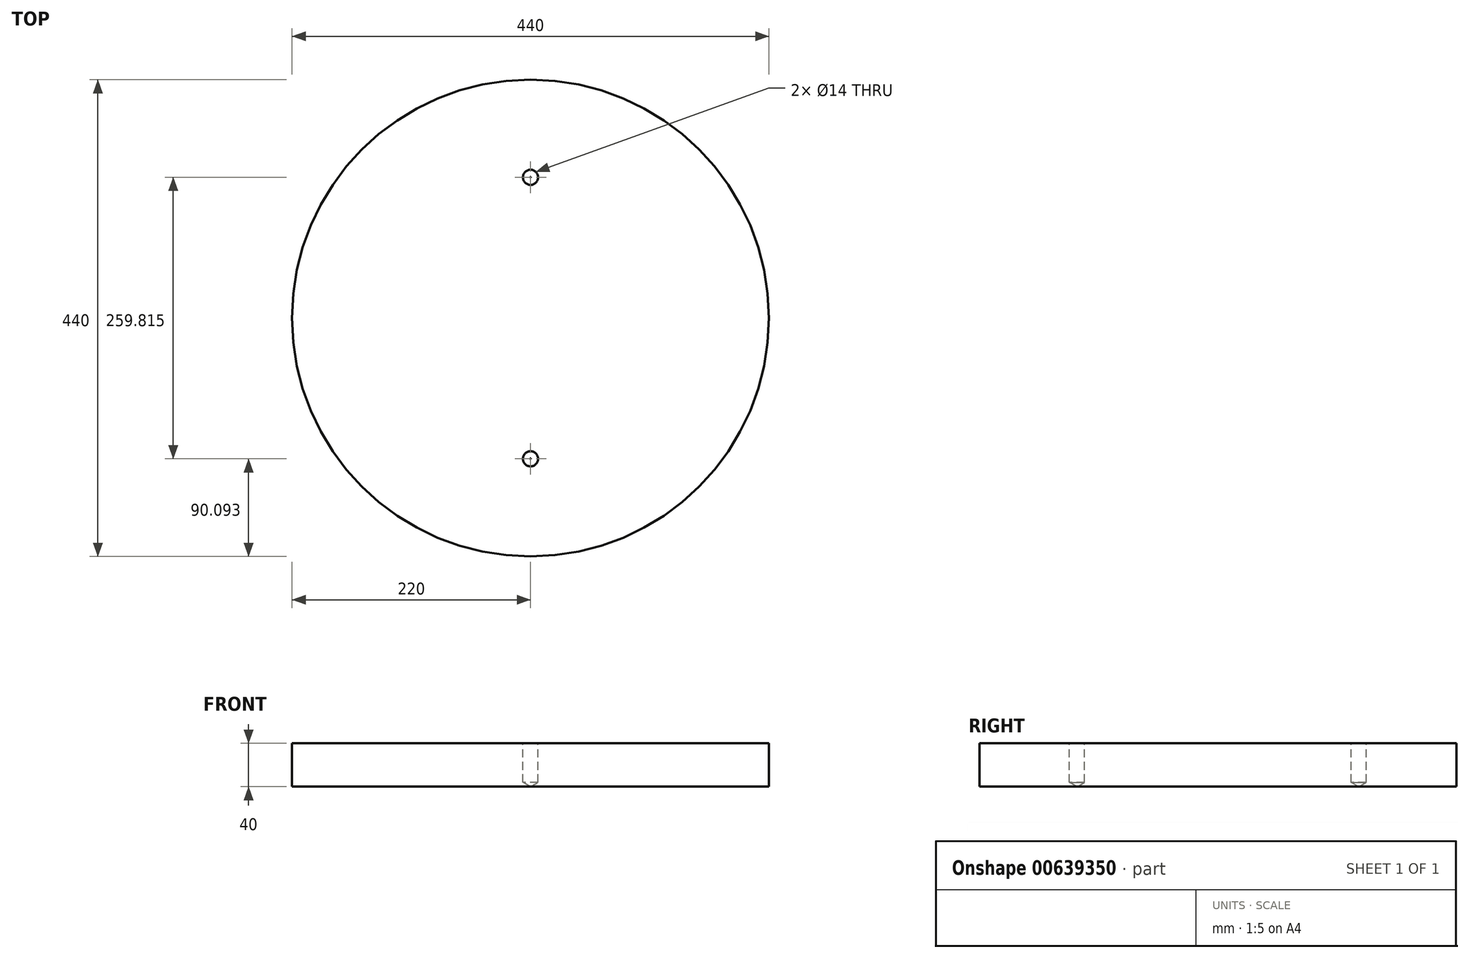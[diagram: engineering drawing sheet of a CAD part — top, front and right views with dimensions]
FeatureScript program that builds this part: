
annotation { "Feature Type Name" : "Feature", "Feature Type Description" : "" }
export const myFeature = defineFeature(function(context is Context, id is Id, definition is map)
    precondition{}
    {
        {
            var Q0;
            Q0=qCreatedBy(makeId("Top.planeOp"),FACE);
            var sketch = newSketch(context, id + "F0", { "sketchPlane" : qUnion([Q0])});
            skCircle(sketch, "E0", {"center": v(0, 0) * mm, "radius": 220 * mm});
            skSolve(sketch);
        }
        {
            var Q0;
            Q0 = qSketchRegion(id + "F0", true);
            extrude(context, id + "F1", {"entities" : qUnion([Q0]), "depth" : 40 * mm, "offsetDistance" : 25 * mm});
        }
        {
            var Q0;
            Q0=makeQuery(id+"F1.opExtrude","CAP_FACE",FACE,{"disambiguationData":[OSD([sQuery(id+"F0.wireOp",EDGE,"E0")])],"isStart":false});
            var sketch = newSketch(context, id + "F2", { "sketchPlane" : qUnion([Q0])});
            skCircle(sketch, "E1", {"center": v(4.9, 0) * mm, "radius": 130 * mm});
            skPoint(sketch, "E2", {"position": v(0, 129.9) * mm});
            skPoint(sketch, "E3", {"position": v(0, -129.9) * mm});
            skSolve(sketch);
        }
        {
            var Q0;
            Q0=sQuery(id+"F2.wireOp",VERTEX,"E2");
            var Q1;
            Q1=sQuery(id+"F2.wireOp",VERTEX,"E3");
            var Q2;
            Q2=makeQuery(id+"F1.opExtrude","SWEPT_BODY",BODY,{"disambiguationData":[OSD([sQuery(id+"F0.wireOp",EDGE,"E0")])]});
            hole(context, id + "F3", {"style" : HoleStyle.SIMPLE, "endStyle" : HoleEndStyle.BLIND, "standardTappedOrClearance" : lookupTablePath({ "standard" : "ISO", "engagement" : "75%", "pitch" : "2 mm", "size" : "M16", "type" : "Tapped" }), "standardBlindInLast" : lookupTablePath({ "standard" : "ISO", "engagement" : "75%", "pitch" : "2 mm", "size" : "M16", "type" : "Tapped" }), "holeDiameter" : 14 * mm, "majorDiameter" : 16 * mm, "showTappedDepth" : true, "holeDepth" : 36 * mm, "tappedDepth" : 30 * mm, "tapClearance" : 3, "locations" : qUnion([Q0, Q1]), "scope" : qUnion([Q2])});
        }
    });
